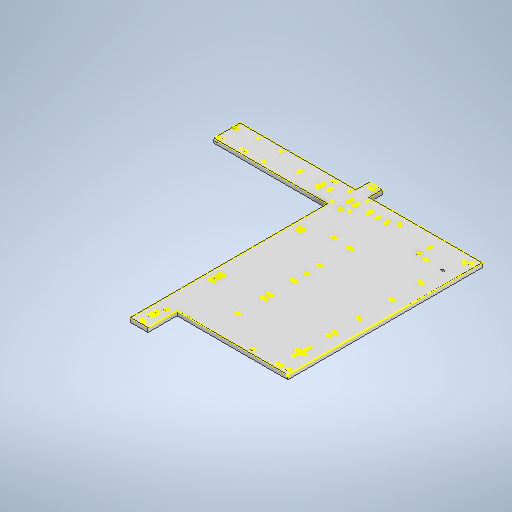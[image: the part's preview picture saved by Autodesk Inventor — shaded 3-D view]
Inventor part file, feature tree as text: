
AUTODESK INVENTOR PART (.ipt)
format: ipt  version: 2025.2 (Build 292293000, 293)  size: 1,568,256 bytes
history: native  units: in
note: dims shown in document units (in); Inventor stores cm internally (conversion verified against a paired STEP export)
features: extrude x26, other x16, sketch x11, hole x5, projected_geometry x4, move_body x3, plane x1, direct_edit x1
ambient origin geometry x8: Origin, YZ Plane, XZ Plane, XY Plane, X Axis, Y Axis, Z Axis, Center Point
bodies: Solid1 (feature_tree)
feature tree (67):
  other  "BoardMounting"
  plane  "Work Plane1"
  sketch  "Sketch2"  dims[d0=0.5in d1=0.5in]
  extrude  "Extrusion4"  Depth=0.5in
  extrude  "ForwardPathDowellPins"  Depth=0.25in
  extrude  "ReversePathDowellPins"  Depth=36.76in
  other  "CTASLMHoles"
  other  "VCSection"
  extrude  "VCPlate"  Depth=0.25in
  hole  "Hole1"  [1 undecoded]
  other  "BaseplateMountingHoles"
  extrude  "BaseplateMountingHolesInner"  Depth=3.175in
  extrude  "BaseplateMountingHolesOuter"  Depth=2.76in
  extrude  "CTASLMElementHolesTop"  Depth=2.577in
  extrude  "Extrusion10"  Depth=7.4961in
  extrude  "Extrusion11"  Depth=1.5in
  sketch  "Sketch8"  dims[d2=0.25in d3=0.4in]
  other  "CylindricalPath"
  other  "CylindricalPathOption1"
  other  "CylindricalPathOption2"
  other  "CylindricalPathOption3"
  other  "CylindricalPathOption3_CTaslmHoles"
  hole  "Hole2"  [1 undecoded]
  extrude  "Extrusion12"  Depth=0.25in
  other  "CylindricalPathOption4"
  hole  "Hole3"  [1 undecoded]
  other  "CylindricalPathOption4_CTaslmHoles"
  extrude  "Extrusion13"  Depth=0.25in
  direct_edit  "Direct Edit1"
  extrude  "CPO4_InnerHolesASLM"  Depth=0.25in
  extrude  "CPO4_InnerHolesCTASLM"  Depth=1.5in
  extrude  "CPO4_OuterHoles"  Depth=0.25in
  extrude  "CPO4_DowellPinsASLM"  Depth=1.5in
  extrude  "CPO4_DowelPinsCTASLM"  Depth=0.25in
  sketch  "Sketch22"  dims[d11=1.5in d12=0.5in]
  extrude  "Extrusion19"  Depth=0.25in
  extrude  "Extrusion20"  Depth=0.25in
  extrude  "Extrusion21"  Depth=0.5in
  extrude  "Extrusion22"  Depth=0.25in
  sketch  "Sketch24"  dims[d15=0.665in d16=2.76in]
  other  "Additional Alignment Holes Top"
  hole  "Hole4"  [1 undecoded]
  extrude  "Extrusion23"  Depth=0.25in
  extrude  "Extrusion24"  Depth=0.25in
  extrude  "Extrusion25"  Depth=0.25in
  sketch  "Sketch27"  dims[d19=10.479in d20=7.4961in]
  extrude  "Extrusion26"  Depth=0.25in
  extrude  "Extrusion27"  Depth=0.25in
  extrude  "Extrusion28"  Depth=0.25in
  hole  "Hole5"  [1 undecoded]
  sketch  "Sketch29"  dims[d23=2.0in d24=0.25in d25=0.197in d26=0.197in d27=0.0797in d28=0.0797in d29=0.25in d30=0.197in d31=0.197in d32=0.0797in d33=0.0797in d34=0.25in d35=0.197in d36=0.197in d37=0.0797in d38=0.0797in d39=0.25in d40=0.197in d41=0.197in d42=0.0797in d43=0.0797in d44=0.25in d45=0.197in d46=0.197in d47=0.0797in d48=0.0797in d49=0.25in d50=0.197in d51=0.197in d52=0.0797in d53=0.0797in d54=0.25in d55=0.197in d56=0.197in d57=0.0797in d58=0.0797in d59=0.25in d60=0.197in d61=0.197in d62=0.0797in d63=0.0797in d64=0.25in d65=0.197in d66=0.197in d67=0.08in d68=0.08in d69=0.25in d70=0.197in d71=0.197in d72=0.08in d73=0.08in d74=0.25in d75=0.197in d76=0.197in d77=0.08in d78=0.08in d81=0.175in d82=0.0in d83=1.5in d84=8.979in d85=1.5in d86=7.4961in d87=6.021in d88=1.0in d89=0.5in d90=0.4738in d91=0.4738in d92=0.25in d93=0.0797in d94=0.0797in d95=0.4738in d96=0.4738in d97=0.25in d98=0.0797in d99=0.0797in d100=0.25in d101=0.197in d102=0.197in d103=0.0797in d104=0.0797in d105=0.25in d106=0.197in d107=0.197in d108=0.0797in d109=0.0797in d110=0.25in d111=0.197in d112=0.0797in d113=0.0797in d114=0.25in d115=0.197in d116=0.0797in d117=0.0797in d118=0.5in d119=1.5in d120=0.5in d121=0.0in d122=0.75in d123=4.857in d124=9.8971in d125=6.8583in d126=1.5in d127=1.5in d128=0.5in d129=1.5in d130=0.25in d131=0.197in d132=0.197in d133=0.0797in d134=0.0797in d135=0.25in d136=0.197in d137=0.197in d138=0.0797in d139=0.0797in d140=0.25in d141=0.197in d142=0.197in d143=0.0797in d144=0.0797in d145=0.175in d146=0.0in d147=9.1809in d148=7.0827in d149=0.25in d150=0.197in d151=0.197in d152=0.0797in d153=0.0797in d154=0.25in d155=0.197in d156=0.197in d157=0.0797in d158=0.0797in d160=0.8752in d161=3.0276in d162=0.1061in d163=0.19in d164=1.5in d165=2.0in d166=1.0in d167=1.0in d168=1.0in d169=0.6in d170=0.5in d171=0.0in d172=0.196in d173=0.5in d174=0.375in d175=0.25in d176=0.5635in d177=1.0in d178=0.8108in d179=21.0in d180=27.0in d181=2.0in d182=14.0in d183=20.0in d184=2.0in d185=19.0in d186=0.4in d187=0.25in d188=0.4in d189=0.25in d190=0.4in d191=0.25in d192=0.4in d193=0.25in d194=0.4in d195=0.25in d196=0.4in d197=0.25in d198=0.4in d199=0.25in d200=0.4in d201=0.25in d202=0.4in d203=0.25in d204=0.4in d205=0.25in d206=0.5in d207=0.0in d208=0.3in d209=0.0in d210=2.0in d211=0.0in d212=0.175in d213=0.0in d214=0.4in d215=0.4in d216=0.4in d217=0.4in d218=0.4in d219=0.4in d220=0.4in d221=0.4in d222=0.4in d223=0.4in d224=0.4in d225=0.4in d226=0.4in d227=0.4in d228=0.4in d229=0.4in d230=0.4in d231=0.4in d232=0.4in d233=0.3in d234=0.0in d235=3.7433in d236=0.25in d237=0.0797in d238=0.0797in d239=0.4in d240=2.5in d241=0.75in d242=0.25in d243=0.0797in d244=0.0797in d245=1.0in d246=1.0in d247=9.1809in d248=7.0827in d249=0.25in d250=0.197in d251=0.197in d252=0.0797in d253=0.0797in d254=0.25in d255=0.197in d256=0.197in d257=0.0797in d258=0.0797in d264=0.25in d265=0.197in d266=0.197in d267=0.0797in d268=0.0797in d269=1.0in d270=1.0in d271=9.8971in d272=6.8583in d273=0.5in d274=1.5in d275=0.25in d276=0.197in d277=0.197in d278=0.0797in d279=0.0797in d280=0.25in d281=0.197in d282=0.197in d283=0.0797in d284=0.0797in d285=0.25in d286=0.197in d287=0.197in d288=0.0797in d289=0.0797in d290=1.0in d291=0.4in d292=0.4in d293=0.4in d294=0.4in d295=0.4in d296=0.4in d297=1.5in d298=0.5in d299=3.0in d300=0.6736in d301=2.7622in d302=1.5in d303=1.5in d304=3.6673in d305=6.9909in d306=1.5in d307=3.9528in d308=0.197in d309=0.197in d310=0.08in d311=0.08in d312=0.25in d313=0.197in d314=0.197in d315=0.08in d316=0.08in d317=0.25in d318=0.197in d319=0.197in d320=0.08in d321=0.08in d322=0.25in d323=0.197in d324=0.197in d325=0.08in d326=0.08in d327=0.25in d328=0.197in d329=0.197in d330=0.08in d331=0.08in d332=0.25in d333=0.197in d334=0.197in d335=0.08in d336=0.08in d337=0.25in d338=0.197in d339=0.197in d340=0.08in d341=0.08in d342=0.25in d343=0.197in d344=0.197in d345=0.08in d346=0.08in d347=0.25in d348=0.197in d349=0.197in d350=0.08in d351=0.08in d352=0.25in d353=0.197in d354=0.197in d355=0.08in d356=0.08in d357=0.25in d358=2.0in d359=0.08in d360=0.08in d361=0.25in d362=0.1509in d363=0.08in d364=0.08in d365=0.25in d366=1.5in d394=4.5in d395=2.4909in d396=0.4738in d397=0.4738in d398=0.25in d399=0.08in d400=0.08in d401=5.4909in d402=0.25in d403=1.5in d404=3.9528in d405=5.4638in d406=9.8801in d407=8.4055in d408=0.1984in d409=0.1984in d410=0.08in d411=0.08in d412=0.25in d413=0.1984in d414=0.1984in d415=0.08in d416=0.08in d417=0.25in d418=0.1984in d419=0.1984in d420=0.08in d421=0.08in d422=0.25in d423=0.4738in d424=0.4738in d425=0.25in d426=0.08in d427=0.08in d428=2.4909in d429=0.25in d430=1.5in d431=3.9528in d432=5.4638in d433=9.8801in d434=8.4055in d435=0.1984in d436=0.1984in d437=0.08in d438=0.08in d439=0.25in d440=0.1984in d441=0.1984in d442=0.08in d443=0.08in d444=0.25in d445=0.1984in d446=0.1984in d447=0.08in d448=0.08in d449=0.25in d450=1.5in d451=0.5in d452=3.0in d453=0.6736in d454=2.7622in d455=1.5in d456=1.5in d457=3.6673in d458=6.9909in d459=1.5in d460=3.9528in d461=0.197in d462=0.197in d463=0.08in d464=0.08in d465=0.25in d466=0.197in d467=0.197in d468=0.08in d469=0.08in d470=0.25in d471=0.197in d472=0.197in d473=0.08in d474=0.08in d475=0.25in d476=0.197in d477=0.197in d478=0.08in d479=0.08in d480=0.25in d481=0.197in d482=0.197in d483=0.08in d484=0.08in d485=0.25in d486=0.197in d487=0.197in d488=0.08in d489=0.08in d490=0.25in d491=0.197in d492=0.197in d493=0.08in d494=0.08in d495=0.25in d496=0.197in d497=0.197in d498=0.08in d499=0.08in d500=0.25in d501=0.197in d502=0.197in d503=0.08in d504=0.08in d505=0.25in d506=0.197in d507=0.197in d508=0.08in d509=0.08in d510=0.25in d511=2.0in d512=0.08in d513=0.08in d514=0.25in d515=0.1509in d516=0.08in d517=0.08in d518=0.25in d519=1.5in d520=4.5in d521=2.4909in d522=0.4738in d523=0.4738in d524=0.25in d525=0.08in d526=0.08in d527=2.4909in d528=0.25in d529=1.5in d530=3.9528in d531=5.4638in d532=9.8801in d533=8.4055in d534=0.1984in d535=0.1984in d536=0.08in d537=0.08in d538=0.25in d539=0.1984in d540=0.1984in d541=0.08in d542=0.08in d543=0.25in d544=0.1984in d545=0.1984in d546=0.08in d547=0.08in d548=0.25in d549=9.1634in d550=8.2568in d551=0.197in d552=0.197in d553=0.08in d554=0.08in d555=0.197in d556=0.197in d557=0.08in d558=0.08in d559=0.197in d560=0.197in d561=0.08in d562=0.08in d563=0.8752in d564=3.0276in d565=0.1061in d566=0.19in d567=1.5in d568=2.0in d569=1.0in d570=1.0in d571=1.0in d572=0.6in d573=0.196in d574=0.5in d575=0.375in d576=0.25in d577=0.5635in d578=1.0in d579=0.8108in d580=1.5in d581=0.5in d582=3.0in d583=0.5in d584=0.0in d585=1.5in d586=0.5in d587=3.0in d588=0.6736in d589=2.7622in d590=1.5in d591=1.5in d592=3.6673in d593=6.9909in d594=1.5in d595=3.9528in d596=0.197in d597=0.197in d598=0.0797in d599=0.0797in d600=0.25in d601=0.197in d602=0.197in d603=0.0797in d604=0.0797in d605=0.25in d606=0.197in d607=0.197in d608=0.0797in d609=0.0797in d610=0.25in d611=0.197in d612=0.197in d613=0.0797in d614=0.0797in d615=0.25in d616=0.197in d617=0.197in d618=0.0797in d619=0.0797in d620=0.25in d621=0.197in d622=0.197in d623=0.0797in d624=0.0797in d625=0.25in d626=0.197in d627=0.197in d628=0.0797in d629=0.0797in d630=0.25in d631=0.197in d632=0.197in d633=0.0797in d634=0.0797in d635=0.25in d636=0.197in d637=0.197in d638=0.0797in d639=0.0797in d640=0.25in d641=0.197in d642=0.197in d643=0.0797in d644=0.0797in d645=0.25in d646=2.0in d647=0.0797in d648=0.0797in d649=0.25in d650=0.1509in d651=0.0797in d652=0.0797in d653=0.25in d654=1.5in d655=4.5in d656=2.4909in d657=0.4738in d658=0.4738in d659=0.25in d660=0.0797in d661=0.0797in d662=2.4909in d663=0.25in d664=1.5in d665=3.9528in d684=0.8752in d685=3.0276in d686=0.1061in d687=0.19in d688=1.5in d689=2.0in d690=1.0in d691=1.0in d692=1.0in d693=0.6in d694=0.196in d695=0.5in d696=0.375in d697=0.25in d698=0.5635in d699=1.0in d700=0.8108in d701=0.75in d704=8.4055in d709=0.25in d714=0.25in d719=0.25in d720=9.1634in d721=8.2568in d722=0.197in d723=0.197in d724=0.0797in d725=0.0797in d726=0.197in d727=0.197in d728=0.0797in d729=0.0797in d730=0.197in d731=0.197in d732=0.0797in d733=0.0797in d734=0.5in d735=0.0in d736=0.0in d737=0.0in d738=-0.5in d739=0.0in d740=0.0in d741=-0.5in d742=0.0in d743=0.0in d744=1.0in d745=0.5in d746=0.0in d747=0.5in d748=0.0in d749=0.4in d750=0.4in d751=0.4in d752=0.4in d753=0.4in d754=0.4in d755=0.4in d756=0.4in d757=0.4in d758=0.4in d759=0.4in d760=0.4in d761=0.4in d762=0.4in d763=0.4in d764=0.4in d765=0.3in d766=0.0in d767=0.0797in d768=0.0797in d769=0.0797in d770=0.0797in d771=0.197in d772=0.0797in d773=0.175in d774=0.0in d775=0.175in d776=0.0in d777=2.5in d778=0.197in d779=0.197in d780=0.197in d781=0.197in d782=0.197in d783=0.197in d784=0.197in d785=0.197in d786=0.0797in d787=0.0797in d788=0.0797in d789=0.0797in d790=0.0797in d791=0.197in d792=0.0797in d793=0.0797in d794=0.0797in d795=0.5in d796=0.75in d797=0.75in d798=0.5in d799=0.0in d800=0.175in d801=0.0in d802=1.0in d803=0.0in d804=0.4in d805=0.3in d806=0.0in d807=0.2382in d808=0.25in d809=0.0797in d810=0.0797in d811=0.75in d812=0.25in d813=0.0797in d814=0.0797in d815=1.0in d816=0.25in d817=0.0797in d818=0.0797in d819=1.0in d820=0.25in d821=0.0797in d822=0.0797in d823=5.0in d824=0.25in d825=0.0797in d826=0.0797in d827=1.0in d828=1.0in d829=1.0in d830=2.0in d831=2.0in d832=0.196in d833=0.5in d834=0.375in d835=0.25in d836=0.5635in d837=1.0in d838=0.8108in d839=1.0in d840=0.0in d841=0.175in d842=0.0in d844=0.4in d845=0.4in d846=0.4in d847=0.4in d848=0.4in d849=0.3in d850=0.0in d853=0.5in d854=0.25in d855=0.5in d856=0.5in d857=0.5in d858=0.25in d859=0.25in d860=0.8661in d861=0.8661in d862=0.8661in d863=0.1191in d864=0.1191in d865=1.0in d866=0.0in d867=0.175in d868=0.0in d869=0.4in d870=0.4in d871=0.3in d872=0.0in d873=0.196in d874=0.5in d875=0.375in d876=0.25in d877=0.5635in d878=1.0in d879=0.8108in d880=0.1576in d881=0.25in d882=0.197in d883=0.197in d884=0.0797in d885=0.0797in d886=0.4in]
  other  "ElementHolesBottom"
  other  "CYlindricalPathOption3_VCHoles"
  sketch  "Sketch16"  dims[d4=4.0in d5=36.76in]
  other  "CylindricalPathOption4_VCHoles"
  sketch  "Sketch20"  dims[d6=0.25in d7=0.4in d8=5.0in]
  other  "MountHolesOuter_CylindricalOption4"
  projected_geometry  "Projected Loop90"
  projected_geometry  "Projected Loop92"
  projected_geometry  "Projected Loop93"
  sketch  "Sketch23"  dims[d13=2.5in d14=3.175in]
  sketch  "Sketch26"  dims[d17=7.104in d18=2.577in]
  sketch  "Sketch28"  dims[d21=1.5in d22=0.1509in]
  projected_geometry  "Projected Loop94"
  move_body  "Move1"
  move_body  "Move2"
  move_body  "Move3"
note: 5 required parameter values undecoded (feature->parameter linkage not recoverable at this tier; creation-order binding heuristic only, values carry confidence <= 0.55)
